AUTODESK INVENTOR PART (.ipt)
format: ipt  version: 2023.5 (Build 275446000, 446)  size: 174,080 bytes
history: native  units: in
note: dims shown in document units (in); Inventor stores cm internally (conversion verified against a paired STEP export)
features: sketch x3
ambient origin geometry x8: Origin, YZ Plane, XZ Plane, XY Plane, X Axis, Y Axis, Z Axis, Center Point
feature tree (3):
  sketch  "Sketch1"  dims[d0=2.0in]
  sketch  "Sketch2"  dims[d1=16.0in]
  sketch  "Sketch3"  dims[d2=0.75in d3=3.0in d4=5.0in d5=5.75in d6=2.0in d7=1.5in d8=8.0in d9=18.0in d10=11.75in d11=7.0in d12=3.7002in d13=8.4959in d14=8.4959in d15=3.7002in d16=4.6651in d18=7.25in d19=2.0in d20=6.0in d21=2.25in d22=2.0in d23=4.0in d25=11.875in d26=4.5in d27=7.5in d28=4.0in d29=0.5in d30=2.0in d31=2.0in d32=5.5in d33=6.5in d34=1.0in d35=1.0in d36=1.0in d37=1.0in d38=4.268in d39=2.315in d40=7.587in d41=5.99in d42=11.25in d43=10.875in d44=14.002in d46=-2.8774in d47=1.722in d48=5.271in d49=10.337in d50=3.0in d51=0.5in d52=4.0in d53=2.0in d54=-2.8774in d55=3.0in d56=4.6651in d57=0.0209in d58=0.0209in d59=9.775in d60=1.8093in d61=1.8093in]
